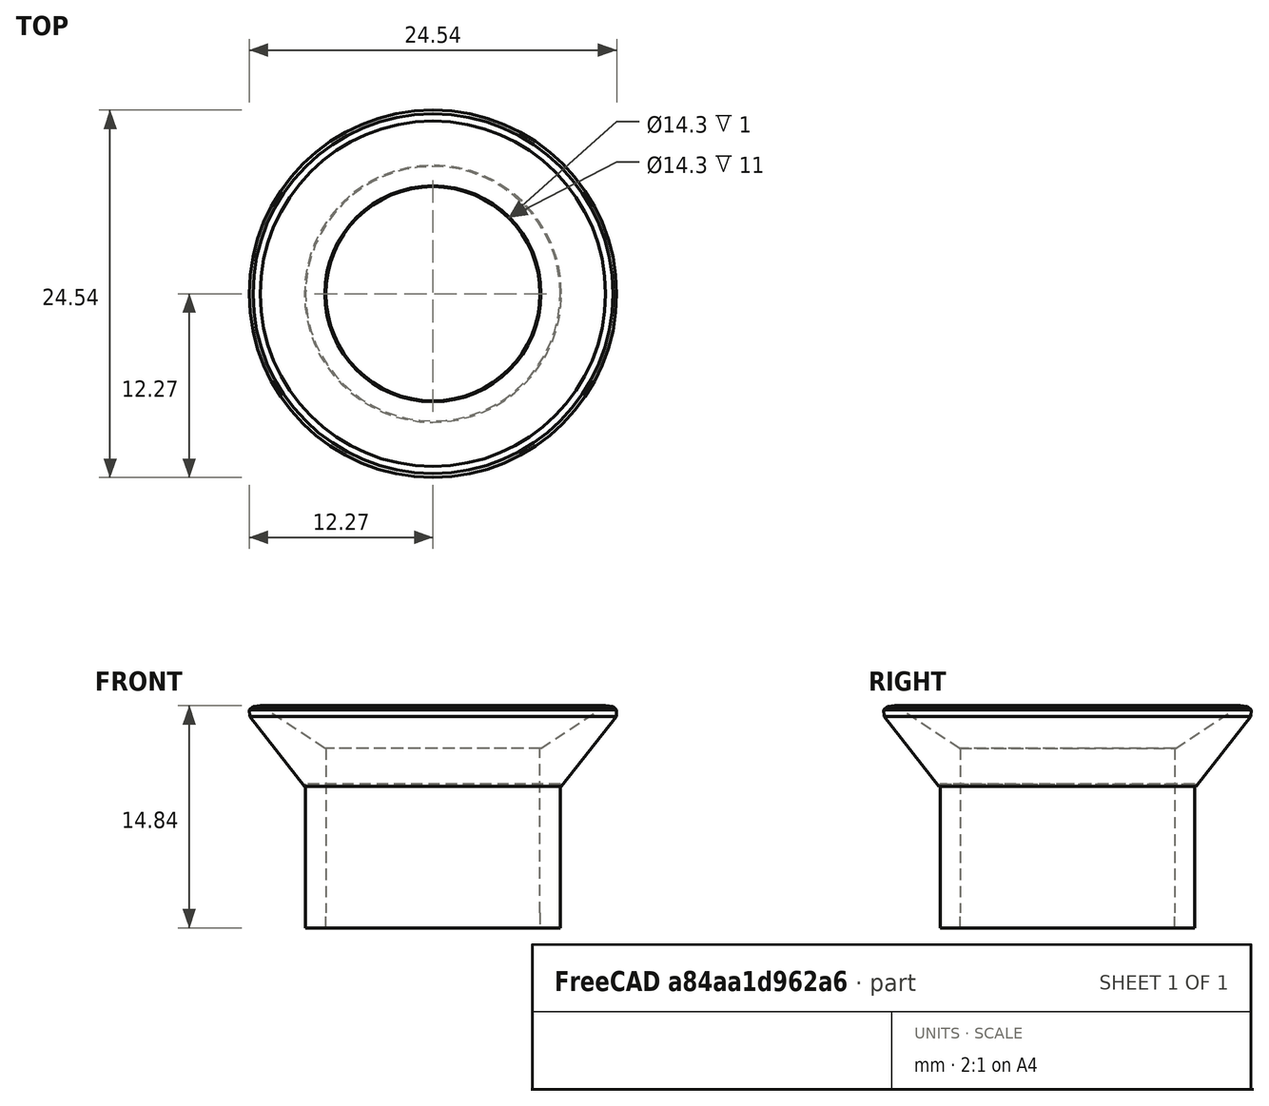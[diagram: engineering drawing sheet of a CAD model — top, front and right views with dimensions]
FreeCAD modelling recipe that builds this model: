
FCSTD DOCUMENT  (FreeCAD 0.19R24267 +99 (Git))
Label: 极光摄像头保护
License: All rights reserved
LicenseURL: http://en.wikipedia.org/wiki/All_rights_reserved
objects: Sketcher::SketchObject×2, PartDesign::Pad×2, PartDesign::Revolution×1, PartDesign::Body×1
note: 9 computed .brp shape members not serialized (recipe doc carries the construction recipe); baked Part::Feature solids carry a one-line shape summary decoded from their .brp

FEATURE [Sketcher::SketchObject] Sketch
  FullyConstrained = true
  MapMode = 5
  Support = -> [XY_Plane]
  sketch-geometry (2):
    g0: Circle CenterX=0 CenterY=0 CenterZ=0 NormalX=0 NormalY=0 NormalZ=1 AngleXU=0 Radius=7.15
    g1: Circle CenterX=0 CenterY=0 CenterZ=0 NormalX=0 NormalY=0 NormalZ=1 AngleXU=0 Radius=8.5
  constraints (4):
    c: Coincident(g0,g-1)
    c: Diameter(g0) = 14.3
    c: Coincident(g1,g0)
    c: Diameter(g1) = 17
FEATURE [PartDesign::Pad] Pad
  Direction = (1,1,1)
  Length = 11
  Length2 = 100
  Profile = -> Sketch
  Type = 0
FEATURE [Sketcher::SketchObject] Sketch001
  FullyConstrained = false
  MapMode = 5
  Placement = pos=(0,0,0) rot=(1,0,0;1.5708rad)
  Support = -> [XZ_Plane]
  sketch-geometry (6):
    g0: LineSegment StartX=7.15423 StartY=10.9593 StartZ=0 EndX=11.5317 EndY=13.8443 EndZ=0
    g1: LineSegment StartX=11.5317 StartY=13.8443 StartZ=0 EndX=12.0165 EndY=13.8027 EndZ=0
    g2: LineSegment StartX=12.0165 StartY=13.8027 StartZ=0 EndX=12.2658 EndY=13.5811 EndZ=0
    g3: LineSegment StartX=12.2658 StartY=13.5811 StartZ=0 EndX=12.2381 EndY=13.124 EndZ=0
    g4: LineSegment StartX=12.2381 StartY=13.124 StartZ=0 EndX=8.58167 EndY=8.45657 EndZ=0
    g5: LineSegment StartX=8.58167 StartY=8.45657 StartZ=0 EndX=7.15423 EndY=10.9593 EndZ=0
  constraints (6):
    c: Coincident(g0,g1)
    c: Coincident(g1,g2)
    c: Coincident(g2,g3)
    c: Coincident(g3,g4)
    c: Coincident(g4,g5)
    c: Coincident(g5,g0)
FEATURE [PartDesign::Revolution] Revolution
  Angle = 360
  Axis = (0,-2e-16,1)
  Base = (0,0,0)
  BaseFeature = -> Pad
  Profile = -> Sketch001
  ReferenceAxis = -> Sketch001 [V_Axis]
  Reversed = true
FEATURE [PartDesign::Pad] Pad001
  BaseFeature = -> Revolution
  Direction = (1,1,1)
  Length = 1
  Length2 = 100
  Profile = -> Revolution [Face2]
  Type = 0
FEATURE [PartDesign::Body] Body
  Group = -> [Sketch,Pad,Sketch001,Revolution,Pad001]
  Origin = -> Origin
  Tip = -> Pad001
